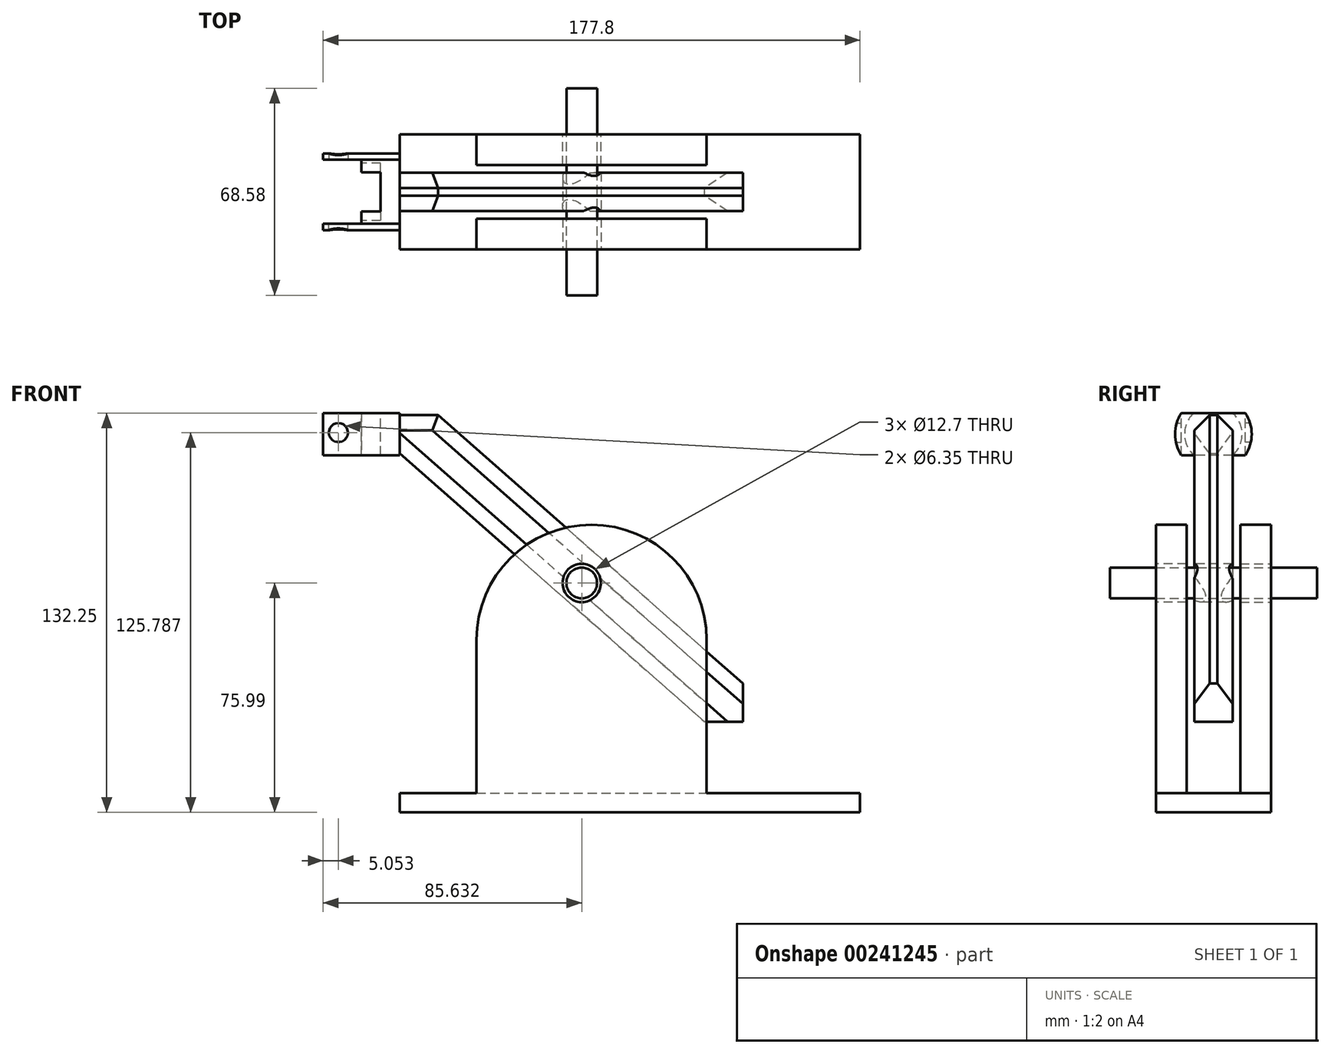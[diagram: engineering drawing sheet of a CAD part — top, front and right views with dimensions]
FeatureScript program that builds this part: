
annotation { "Feature Type Name" : "Feature", "Feature Type Description" : "" }
export const myFeature = defineFeature(function(context is Context, id is Id, definition is map)
    precondition{}
    {
        {
            var Q0;
            Q0=qCreatedBy(makeId("Front.planeOp"),FACE);
            var sketch = newSketch(context, id + "F0", { "sketchPlane" : qUnion([Q0])});
            skLineSegment(sketch, "E0.bottom", {"start": v(-76.2, 55.62) * mm, "end": v(37.4, 55.62) * mm});
            skLineSegment(sketch, "E0.top", {"start": v(-76.2, -45.98) * mm, "end": v(37.4, -45.98) * mm});
            skLineSegment(sketch, "E0.left", {"start": v(-76.2, 55.62) * mm, "end": v(-76.2, -45.98) * mm});
            skLineSegment(sketch, "E0.right", {"start": v(37.4, 55.62) * mm, "end": v(37.4, -45.98) * mm});
            skLineSegment(sketch, "E1", {"start": v(-76.2, 42.92) * mm, "end": v(24.7, -45.98) * mm});
            skLineSegment(sketch, "E2", {"start": v(37.4, -33.28) * mm, "end": v(-63.5, 55.62) * mm});
            skSolve(sketch);
        }
        {
            var Q0;
            {var subQ7=sQuery(id+"F0.wireOp",EDGE,"E1");Q0=makeQuery(id+"F0.imprint","IMPRINT",FACE,{"disambiguationData":[TD([[makeQuery(id+"F0.imprint","IMPRINT",EDGE,{"derivedFrom":subQ7}),1.0]])]});}
            extrude(context, id + "F1", {"entities" : qUnion([Q0]), "depth" : 12.7 * mm});
        }
        {
            var Q0;
            Q0=makeQuery(id+"F1.opExtrude","SWEPT_FACE",FACE,{"disambiguationData":[OSD([sQuery(id+"F0.wireOp",EDGE,"E0.left")])]});
            var sketch = newSketch(context, id + "F2", { "sketchPlane" : qUnion([Q0])});
            skLineSegment(sketch, "E3.bottom", {"start": v(0, 55.62) * mm, "end": v(12.7, 55.62) * mm});
            skLineSegment(sketch, "E3.top", {"start": v(0, 42.92) * mm, "end": v(12.7, 42.92) * mm});
            skLineSegment(sketch, "E3.left", {"start": v(0, 55.62) * mm, "end": v(0, 42.92) * mm});
            skLineSegment(sketch, "E3.right", {"start": v(12.7, 55.62) * mm, "end": v(12.7, 42.92) * mm});
            skSolve(sketch);
        }
        {
            var Q0;
            Q0 = qSketchRegion(id + "F2", true);
            extrude(context, id + "F3", {"entities" : qUnion([Q0]), "operationType" : NewBodyOperationType.ADD, "depth" : 12.7 * mm});
        }
        {
            var Q0;
            Q0=makeQuery(id+"F3.boolean.opBoolean","MERGE",FACE,{"derivedFrom":[makeQuery(id+"F1.opExtrude","CAP_FACE",FACE,{"disambiguationData":[OSD([sQuery(id+"F0.wireOp",EDGE,"E0.bottom"),sQuery(id+"F0.wireOp",EDGE,"E0.top"),sQuery(id+"F0.wireOp",EDGE,"E0.left"),sQuery(id+"F0.wireOp",EDGE,"E0.right"),sQuery(id+"F0.wireOp",EDGE,"E1"),sQuery(id+"F0.wireOp",EDGE,"E2")])],"isStart":true}),makeQuery(id+"F3.opExtrude","SWEPT_FACE",FACE,{"disambiguationData":[OSD([sQuery(id+"F2.wireOp",EDGE,"E3.left")])]})]});
            var sketch = newSketch(context, id + "F4", { "sketchPlane" : qUnion([Q0])});
            skLineSegment(sketch, "E4.bottom", {"start": v(76.2, 55.62) * mm, "end": v(88.9, 55.62) * mm});
            skLineSegment(sketch, "E4.top", {"start": v(76.2, 42.92) * mm, "end": v(88.9, 42.92) * mm});
            skLineSegment(sketch, "E4.left", {"start": v(76.2, 55.62) * mm, "end": v(76.2, 42.92) * mm});
            skLineSegment(sketch, "E4.right", {"start": v(88.9, 55.62) * mm, "end": v(88.9, 42.92) * mm});
            skSolve(sketch);
        }
        {
            var Q0;
            Q0 = qSketchRegion(id + "F4", true);
            extrude(context, id + "F5", {"entities" : qUnion([Q0]), "operationType" : NewBodyOperationType.ADD, "depth" : 6.35 * mm});
        }
        {
            var Q0;
            Q0=makeQuery(id+"F3.boolean.opBoolean","MERGE",FACE,{"derivedFrom":[makeQuery(id+"F1.opExtrude","CAP_FACE",FACE,{"disambiguationData":[OSD([sQuery(id+"F0.wireOp",EDGE,"E0.bottom"),sQuery(id+"F0.wireOp",EDGE,"E0.top"),sQuery(id+"F0.wireOp",EDGE,"E0.left"),sQuery(id+"F0.wireOp",EDGE,"E0.right"),sQuery(id+"F0.wireOp",EDGE,"E1"),sQuery(id+"F0.wireOp",EDGE,"E2")])],"isStart":false}),makeQuery(id+"F3.opExtrude","SWEPT_FACE",FACE,{"disambiguationData":[OSD([sQuery(id+"F2.wireOp",EDGE,"E3.right")])]})]});
            var sketch = newSketch(context, id + "F6", { "sketchPlane" : qUnion([Q0])});
            skLineSegment(sketch, "E5.bottom", {"start": v(-76.2, 55.62) * mm, "end": v(-88.9, 55.62) * mm});
            skLineSegment(sketch, "E5.top", {"start": v(-76.2, 42.92) * mm, "end": v(-88.9, 42.92) * mm});
            skLineSegment(sketch, "E5.left", {"start": v(-76.2, 55.62) * mm, "end": v(-76.2, 42.92) * mm});
            skLineSegment(sketch, "E5.right", {"start": v(-88.9, 55.62) * mm, "end": v(-88.9, 42.92) * mm});
            skSolve(sketch);
        }
        {
            var Q0;
            Q0 = qSketchRegion(id + "F6", true);
            extrude(context, id + "F7", {"entities" : qUnion([Q0]), "operationType" : NewBodyOperationType.ADD, "depth" : 6.35 * mm});
        }
        {
            var Q0;
            Q0=makeQuery(id+"F7.boolean.opBoolean","MERGE",FACE,{"derivedFrom":[makeQuery(id+"F5.boolean.opBoolean","MERGE",FACE,{"derivedFrom":[makeQuery(id+"F3.boolean.opBoolean","MERGE",FACE,{"derivedFrom":[makeQuery(id+"F1.opExtrude","SWEPT_FACE",FACE,{"disambiguationData":[OSD([sQuery(id+"F0.wireOp",EDGE,"E0.bottom")])]}),makeQuery(id+"F3.opExtrude","SWEPT_FACE",FACE,{"disambiguationData":[OSD([sQuery(id+"F2.wireOp",EDGE,"E3.bottom")])]})]}),makeQuery(id+"F5.opExtrude","SWEPT_FACE",FACE,{"disambiguationData":[OSD([sQuery(id+"F4.wireOp",EDGE,"E4.bottom")])]})]}),makeQuery(id+"F7.opExtrude","SWEPT_FACE",FACE,{"disambiguationData":[OSD([sQuery(id+"F6.wireOp",EDGE,"E5.bottom")])]})]});
            var sketch = newSketch(context, id + "F8", { "sketchPlane" : qUnion([Q0])});
            skLineSegment(sketch, "E6.bottom", {"start": v(-76.2, 6.35) * mm, "end": v(-88.9, 6.35) * mm});
            skLineSegment(sketch, "E6.top", {"start": v(-76.2, -19.05) * mm, "end": v(-88.9, -19.05) * mm});
            skLineSegment(sketch, "E6.left", {"start": v(-76.2, 6.35) * mm, "end": v(-76.2, -19.05) * mm});
            skLineSegment(sketch, "E6.right", {"start": v(-88.9, 6.35) * mm, "end": v(-88.9, -19.05) * mm});
            skSolve(sketch);
        }
        {
            var Q0;
            Q0 = qSketchRegion(id + "F8", true);
            extrude(context, id + "F9", {"entities" : qUnion([Q0]), "operationType" : NewBodyOperationType.ADD, "depth" : 6.35 * mm});
        }
        {
            var Q0;
            Q0=makeQuery(id+"F7.boolean.opBoolean","MERGE",FACE,{"derivedFrom":[makeQuery(id+"F5.boolean.opBoolean","MERGE",FACE,{"derivedFrom":[makeQuery(id+"F3.opExtrude","SWEPT_FACE",FACE,{"disambiguationData":[OSD([sQuery(id+"F2.wireOp",EDGE,"E3.top")])]}),makeQuery(id+"F5.opExtrude","SWEPT_FACE",FACE,{"disambiguationData":[OSD([sQuery(id+"F4.wireOp",EDGE,"E4.top")])]})]}),makeQuery(id+"F7.opExtrude","SWEPT_FACE",FACE,{"disambiguationData":[OSD([sQuery(id+"F6.wireOp",EDGE,"E5.top")])]})]});
            extrude(context, id + "F10", {"entities" : qUnion([Q0]), "operationType" : NewBodyOperationType.ADD, "depth" : 6.35 * mm});
        }
        {
            var Q0;
            {var subQ0=sQuery(id+"F6.wireOp",EDGE,"E5.right");var subQ1=sQuery(id+"F4.wireOp",EDGE,"E4.right");var subQ2=sQuery(id+"F2.wireOp",EDGE,"E3.top");Q0=makeQuery(id+"F10.boolean.opBoolean","MERGE",FACE,{"derivedFrom":[makeQuery(id+"F9.boolean.opBoolean","MERGE",FACE,{"derivedFrom":[makeQuery(id+"F7.boolean.opBoolean","MERGE",FACE,{"derivedFrom":[makeQuery(id+"F5.boolean.opBoolean","MERGE",FACE,{"derivedFrom":[makeQuery(id+"F3.opExtrude","CAP_FACE",FACE,{"disambiguationData":[OSD([sQuery(id+"F2.wireOp",EDGE,"E3.bottom"),subQ2,sQuery(id+"F2.wireOp",EDGE,"E3.left"),sQuery(id+"F2.wireOp",EDGE,"E3.right")])],"isStart":false}),makeQuery(id+"F5.opExtrude","SWEPT_FACE",FACE,{"disambiguationData":[OSD([subQ1])]})]}),makeQuery(id+"F7.opExtrude","SWEPT_FACE",FACE,{"disambiguationData":[OSD([subQ0])]})]}),makeQuery(id+"F9.opExtrude","SWEPT_FACE",FACE,{"disambiguationData":[OSD([sQuery(id+"F8.wireOp",EDGE,"E6.right")])]})]}),makeQuery(id+"F10.opExtrude","SWEPT_FACE",FACE,{"disambiguationData":[OSD([subQ2,sQuery(id+"F4.wireOp",EDGE,"E4.top"),subQ1,sQuery(id+"F6.wireOp",EDGE,"E5.top"),subQ0])]})]});}
            var sketch = newSketch(context, id + "F11", { "sketchPlane" : qUnion([Q0])});
            skCircle(sketch, "E7", {"center": v(6.35, 49.27) * mm, "radius": 12.7 * mm});
            skPoint(sketch, "E7.centerSnap0", {"position": v(6.35, 36.57) * mm});
            skSolve(sketch);
        }
        {
            var Q0;
            {var subQ0=sQuery(id+"F11.wireOp",EDGE,"E7");var subQ1=sQuery(id+"F8.wireOp",EDGE,"E6.right");var subQ2=makeQuery(id+"F9.opExtrude","CAP_EDGE",EDGE,{"disambiguationData":[OSD([subQ1])],"isStart":false});var subQ3=makeQuery(id+"F11.imprint","INTERSECT",VERTEX,{"derivedFrom":[subQ2,subQ0]});Q0=makeQuery(id+"F11.imprint","IMPRINT",FACE,{"disambiguationData":[TD([[makeQuery(id+"F11.imprint","IMPRINT",EDGE,{"disambiguationData":[TD([[subQ3,-1.0]])],"derivedFrom":subQ0}),-1.0]])]});}
            var Q1;
            {var subQ0=sQuery(id+"F11.wireOp",EDGE,"E7");var subQ1=sQuery(id+"F8.wireOp",EDGE,"E6.right");var subQ2=makeQuery(id+"F9.opExtrude","CAP_EDGE",EDGE,{"disambiguationData":[OSD([subQ1])],"isStart":false});var subQ3=makeQuery(id+"F11.imprint","INTERSECT",VERTEX,{"derivedFrom":[subQ2,subQ0]});Q1=makeQuery(id+"F11.imprint","IMPRINT",FACE,{"disambiguationData":[TD([[makeQuery(id+"F11.imprint","IMPRINT",EDGE,{"disambiguationData":[TD([[subQ3,1.0]])],"derivedFrom":subQ0}),-1.0]])]});}
            var Q2;
            {var subQ0=sQuery(id+"F11.wireOp",EDGE,"E7");var subQ1=sQuery(id+"F6.wireOp",EDGE,"E5.right");var subQ2=sQuery(id+"F6.wireOp",EDGE,"E5.top");var subQ3=makeQuery(id+"F10.boolean.opBoolean","MERGE",EDGE,{"derivedFrom":[makeQuery(id+"F9.boolean.opBoolean","MERGE",EDGE,{"derivedFrom":[makeQuery(id+"F7.opExtrude","CAP_EDGE",EDGE,{"disambiguationData":[OSD([subQ1])],"isStart":false}),makeQuery(id+"F9.opExtrude","SWEPT_EDGE",EDGE,{"disambiguationData":[OSD([sQuery(id+"F8.wireOp",EDGE,"E6.top"),sQuery(id+"F8.wireOp",EDGE,"E6.right")])]})]}),makeQuery(id+"F10.opExtrude","SWEPT_EDGE",EDGE,{"disambiguationData":[OSD([subQ2,subQ1])]})]});var subQ4=makeQuery(id+"F11.imprint","INTERSECT",VERTEX,{"derivedFrom":[subQ3,subQ0]});Q2=makeQuery(id+"F11.imprint","IMPRINT",FACE,{"disambiguationData":[TD([[makeQuery(id+"F11.imprint","IMPRINT",EDGE,{"disambiguationData":[TD([[subQ4,1.0]])],"derivedFrom":subQ0}),-1.0]])]});}
            var Q3;
            {var subQ0=sQuery(id+"F11.wireOp",EDGE,"E7");var subQ1=sQuery(id+"F4.wireOp",EDGE,"E4.right");var subQ2=sQuery(id+"F4.wireOp",EDGE,"E4.top");var subQ3=makeQuery(id+"F10.boolean.opBoolean","MERGE",EDGE,{"derivedFrom":[makeQuery(id+"F9.boolean.opBoolean","MERGE",EDGE,{"derivedFrom":[makeQuery(id+"F5.opExtrude","CAP_EDGE",EDGE,{"disambiguationData":[OSD([subQ1])],"isStart":false}),makeQuery(id+"F9.opExtrude","SWEPT_EDGE",EDGE,{"disambiguationData":[OSD([sQuery(id+"F8.wireOp",EDGE,"E6.bottom"),sQuery(id+"F8.wireOp",EDGE,"E6.right")])]})]}),makeQuery(id+"F10.opExtrude","SWEPT_EDGE",EDGE,{"disambiguationData":[OSD([subQ2,subQ1])]})]});var subQ4=makeQuery(id+"F11.imprint","INTERSECT",VERTEX,{"derivedFrom":[subQ3,subQ0]});Q3=makeQuery(id+"F11.imprint","IMPRINT",FACE,{"disambiguationData":[TD([[makeQuery(id+"F11.imprint","IMPRINT",EDGE,{"disambiguationData":[TD([[subQ4,-1.0]])],"derivedFrom":subQ0}),-1.0]])]});}
            extrude(context, id + "F12", {"entities" : qUnion([Q0, Q1, Q2, Q3]), "operationType" : NewBodyOperationType.REMOVE, "oppositeDirection" : true, "depth" : 12.7 * mm});
        }
        {
            var Q0;
            Q0=makeQuery(id+"F3.boolean.opBoolean","MERGE",EDGE,{"derivedFrom":[makeQuery(id+"F1.opExtrude","CAP_EDGE",EDGE,{"disambiguationData":[OSD([sQuery(id+"F0.wireOp",EDGE,"E0.bottom")])],"isStart":true}),makeQuery(id+"F3.opExtrude","SWEPT_EDGE",EDGE,{"disambiguationData":[OSD([sQuery(id+"F2.wireOp",EDGE,"E3.bottom"),sQuery(id+"F2.wireOp",EDGE,"E3.left")])]})]});
            var Q1;
            Q1=makeQuery(id+"F1.opExtrude","CAP_EDGE",EDGE,{"disambiguationData":[OSD([sQuery(id+"F0.wireOp",EDGE,"E2")])],"isStart":false});
            var Q2;
            Q2=makeQuery(id+"F3.boolean.opBoolean","MERGE",EDGE,{"derivedFrom":[makeQuery(id+"F1.opExtrude","CAP_EDGE",EDGE,{"disambiguationData":[OSD([sQuery(id+"F0.wireOp",EDGE,"E0.bottom")])],"isStart":false}),makeQuery(id+"F3.opExtrude","SWEPT_EDGE",EDGE,{"disambiguationData":[OSD([sQuery(id+"F2.wireOp",EDGE,"E3.bottom"),sQuery(id+"F2.wireOp",EDGE,"E3.right")])]})]});
            var Q3;
            Q3=makeQuery(id+"F1.opExtrude","CAP_EDGE",EDGE,{"disambiguationData":[OSD([sQuery(id+"F0.wireOp",EDGE,"E2")])],"isStart":true});
            var Q4;
            Q4=makeQuery(id+"F1.opExtrude","CAP_EDGE",EDGE,{"disambiguationData":[OSD([sQuery(id+"F0.wireOp",EDGE,"E1")])],"isStart":true});
            var Q5;
            Q5=makeQuery(id+"F1.opExtrude","CAP_EDGE",EDGE,{"disambiguationData":[OSD([sQuery(id+"F0.wireOp",EDGE,"E1")])],"isStart":false});
            chamfer(context, id + "F13", {"entities" : qUnion([Q0, Q1, Q2, Q3, Q4, Q5]), "width" : 5.08 * mm, "tangentPropagation" : true});
        }
        {
            var Q0;
            {var subQ0=sQuery(id+"F6.wireOp",EDGE,"E5.right");var subQ1=sQuery(id+"F4.wireOp",EDGE,"E4.right");var subQ2=sQuery(id+"F2.wireOp",EDGE,"E3.top");Q0=makeQuery(id+"F10.boolean.opBoolean","MERGE",FACE,{"derivedFrom":[makeQuery(id+"F9.boolean.opBoolean","MERGE",FACE,{"derivedFrom":[makeQuery(id+"F7.boolean.opBoolean","MERGE",FACE,{"derivedFrom":[makeQuery(id+"F5.boolean.opBoolean","MERGE",FACE,{"derivedFrom":[makeQuery(id+"F3.opExtrude","CAP_FACE",FACE,{"disambiguationData":[OSD([sQuery(id+"F2.wireOp",EDGE,"E3.bottom"),subQ2,sQuery(id+"F2.wireOp",EDGE,"E3.left"),sQuery(id+"F2.wireOp",EDGE,"E3.right")])],"isStart":false}),makeQuery(id+"F5.opExtrude","SWEPT_FACE",FACE,{"disambiguationData":[OSD([subQ1])]})]}),makeQuery(id+"F7.opExtrude","SWEPT_FACE",FACE,{"disambiguationData":[OSD([subQ0])]})]}),makeQuery(id+"F9.opExtrude","SWEPT_FACE",FACE,{"disambiguationData":[OSD([sQuery(id+"F8.wireOp",EDGE,"E6.right")])]})]}),makeQuery(id+"F10.opExtrude","SWEPT_FACE",FACE,{"disambiguationData":[OSD([subQ2,sQuery(id+"F4.wireOp",EDGE,"E4.top"),subQ1,sQuery(id+"F6.wireOp",EDGE,"E5.top"),subQ0])]})]});}
            var sketch = newSketch(context, id + "F14", { "sketchPlane" : qUnion([Q0])});
            skCircle(sketch, "E8", {"center": v(6.35, 49.27) * mm, "radius": 9.53 * mm});
            skSolve(sketch);
        }
        {
            var Q0;
            Q0=makeQuery(id+"F14.imprint","IMPRINT",FACE,{"disambiguationData":[TD([[makeQuery(id+"F14.imprint","IMPRINT",EDGE,{"derivedFrom":sQuery(id+"F14.wireOp",EDGE,"E8")}),1.0]])]});
            var sketch = newSketch(context, id + "F15", { "sketchPlane" : qUnion([Q0])});
            skSolve(sketch);
        }
        {
            var Q0;
            Q0 = qSketchRegion(id + "F15", true);
            var Q1;
            Q1=makeQuery(id+"F14.imprint","IMPRINT",FACE,{"disambiguationData":[TD([[makeQuery(id+"F14.imprint","IMPRINT",EDGE,{"derivedFrom":sQuery(id+"F14.wireOp",EDGE,"E8")}),1.0]])]});
            extrude(context, id + "F16", {"entities" : qUnion([Q0, Q1]), "operationType" : NewBodyOperationType.REMOVE, "oppositeDirection" : true, "depth" : 6.35 * mm});
        }
        {
            var Q0;
            {var subQ0=sQuery(id+"F6.wireOp",EDGE,"E5.right");var subQ1=sQuery(id+"F4.wireOp",EDGE,"E4.right");var subQ2=sQuery(id+"F2.wireOp",EDGE,"E3.top");Q0=makeQuery(id+"F10.boolean.opBoolean","MERGE",FACE,{"derivedFrom":[makeQuery(id+"F9.boolean.opBoolean","MERGE",FACE,{"derivedFrom":[makeQuery(id+"F7.boolean.opBoolean","MERGE",FACE,{"derivedFrom":[makeQuery(id+"F5.boolean.opBoolean","MERGE",FACE,{"derivedFrom":[makeQuery(id+"F3.opExtrude","CAP_FACE",FACE,{"disambiguationData":[OSD([sQuery(id+"F2.wireOp",EDGE,"E3.bottom"),subQ2,sQuery(id+"F2.wireOp",EDGE,"E3.left"),sQuery(id+"F2.wireOp",EDGE,"E3.right")])],"isStart":false}),makeQuery(id+"F5.opExtrude","SWEPT_FACE",FACE,{"disambiguationData":[OSD([subQ1])]})]}),makeQuery(id+"F7.opExtrude","SWEPT_FACE",FACE,{"disambiguationData":[OSD([subQ0])]})]}),makeQuery(id+"F9.opExtrude","SWEPT_FACE",FACE,{"disambiguationData":[OSD([sQuery(id+"F8.wireOp",EDGE,"E6.right")])]})]}),makeQuery(id+"F10.opExtrude","SWEPT_FACE",FACE,{"disambiguationData":[OSD([subQ2,sQuery(id+"F4.wireOp",EDGE,"E4.top"),subQ1,sQuery(id+"F6.wireOp",EDGE,"E5.top"),subQ0])]})]});}
            var sketch = newSketch(context, id + "F17", { "sketchPlane" : qUnion([Q0])});
            skLineSegment(sketch, "E9.bottom", {"start": v(-4.26, 56.26) * mm, "end": v(16.96, 56.26) * mm});
            skLineSegment(sketch, "E9.top", {"start": v(-4.26, 63.12) * mm, "end": v(16.96, 63.12) * mm});
            skLineSegment(sketch, "E9.left", {"start": v(-4.26, 56.26) * mm, "end": v(-4.26, 63.12) * mm});
            skLineSegment(sketch, "E9.right", {"start": v(16.96, 56.26) * mm, "end": v(16.96, 63.12) * mm});
            skLineSegment(sketch, "E10.bottom", {"start": v(-4.26, 42.29) * mm, "end": v(17.6, 42.29) * mm});
            skLineSegment(sketch, "E10.top", {"start": v(-4.26, 35.94) * mm, "end": v(17.6, 35.94) * mm});
            skLineSegment(sketch, "E10.left", {"start": v(-4.26, 42.29) * mm, "end": v(-4.26, 35.94) * mm});
            skLineSegment(sketch, "E10.right", {"start": v(17.6, 42.29) * mm, "end": v(17.6, 35.94) * mm});
            skSolve(sketch);
        }
        {
            var Q0;
            Q0 = qSketchRegion(id + "F17", true);
            extrude(context, id + "F18", {"entities" : qUnion([Q0]), "operationType" : NewBodyOperationType.REMOVE, "oppositeDirection" : true, "depth" : 12.7 * mm});
        }
        {
            var Q0;
            {var subQ0=sQuery(id+"F6.wireOp",EDGE,"E5.right");var subQ1=sQuery(id+"F4.wireOp",EDGE,"E4.right");var subQ2=sQuery(id+"F2.wireOp",EDGE,"E3.top");Q0=makeQuery(id+"F18.boolean.opBoolean","SPLIT",FACE,{"disambiguationData":[OD(0.0)],"derivedFrom":makeQuery(id+"F10.boolean.opBoolean","MERGE",FACE,{"derivedFrom":[makeQuery(id+"F9.boolean.opBoolean","MERGE",FACE,{"derivedFrom":[makeQuery(id+"F7.boolean.opBoolean","MERGE",FACE,{"derivedFrom":[makeQuery(id+"F5.boolean.opBoolean","MERGE",FACE,{"derivedFrom":[makeQuery(id+"F3.opExtrude","CAP_FACE",FACE,{"disambiguationData":[OSD([sQuery(id+"F2.wireOp",EDGE,"E3.bottom"),subQ2,sQuery(id+"F2.wireOp",EDGE,"E3.left"),sQuery(id+"F2.wireOp",EDGE,"E3.right")])],"isStart":false}),makeQuery(id+"F5.opExtrude","SWEPT_FACE",FACE,{"disambiguationData":[OSD([subQ1])]})]}),makeQuery(id+"F7.opExtrude","SWEPT_FACE",FACE,{"disambiguationData":[OSD([subQ0])]})]}),makeQuery(id+"F9.opExtrude","SWEPT_FACE",FACE,{"disambiguationData":[OSD([sQuery(id+"F8.wireOp",EDGE,"E6.right")])]})]}),makeQuery(id+"F10.opExtrude","SWEPT_FACE",FACE,{"disambiguationData":[OSD([subQ2,sQuery(id+"F4.wireOp",EDGE,"E4.top"),subQ1,sQuery(id+"F6.wireOp",EDGE,"E5.top"),subQ0])]})]})});}
            var Q1;
            {var subQ0=sQuery(id+"F6.wireOp",EDGE,"E5.right");var subQ1=sQuery(id+"F4.wireOp",EDGE,"E4.right");var subQ2=sQuery(id+"F2.wireOp",EDGE,"E3.top");Q1=makeQuery(id+"F18.boolean.opBoolean","SPLIT",FACE,{"disambiguationData":[OD(1.0)],"derivedFrom":makeQuery(id+"F10.boolean.opBoolean","MERGE",FACE,{"derivedFrom":[makeQuery(id+"F9.boolean.opBoolean","MERGE",FACE,{"derivedFrom":[makeQuery(id+"F7.boolean.opBoolean","MERGE",FACE,{"derivedFrom":[makeQuery(id+"F5.boolean.opBoolean","MERGE",FACE,{"derivedFrom":[makeQuery(id+"F3.opExtrude","CAP_FACE",FACE,{"disambiguationData":[OSD([sQuery(id+"F2.wireOp",EDGE,"E3.bottom"),subQ2,sQuery(id+"F2.wireOp",EDGE,"E3.left"),sQuery(id+"F2.wireOp",EDGE,"E3.right")])],"isStart":false}),makeQuery(id+"F5.opExtrude","SWEPT_FACE",FACE,{"disambiguationData":[OSD([subQ1])]})]}),makeQuery(id+"F7.opExtrude","SWEPT_FACE",FACE,{"disambiguationData":[OSD([subQ0])]})]}),makeQuery(id+"F9.opExtrude","SWEPT_FACE",FACE,{"disambiguationData":[OSD([sQuery(id+"F8.wireOp",EDGE,"E6.right")])]})]}),makeQuery(id+"F10.opExtrude","SWEPT_FACE",FACE,{"disambiguationData":[OSD([subQ2,sQuery(id+"F4.wireOp",EDGE,"E4.top"),subQ1,sQuery(id+"F6.wireOp",EDGE,"E5.top"),subQ0])]})]})});}
            extrude(context, id + "F19", {"entities" : qUnion([Q0, Q1]), "operationType" : NewBodyOperationType.ADD, "depth" : 12.7 * mm});
        }
        {
            var Q0;
            Q0=makeQuery(id+"F15.imprint","IMPRINT",FACE,{"disambiguationData":[TD([[makeQuery(id+"F15.imprint","IMPRINT",EDGE,{"derivedFrom":makeQuery(id+"F14.imprint","IMPRINT",EDGE,{"derivedFrom":sQuery(id+"F14.wireOp",EDGE,"E8")})}),1.0]])]});
            var sketch = newSketch(context, id + "F20", { "sketchPlane" : qUnion([Q0])});
            skLineSegment(sketch, "E11.bottom", {"start": v(-4.26, 56.26) * mm, "end": v(16.96, 56.26) * mm});
            skLineSegment(sketch, "E11.top", {"start": v(-4.26, 42.29) * mm, "end": v(16.96, 42.29) * mm});
            skLineSegment(sketch, "E11.left", {"start": v(-4.26, 56.26) * mm, "end": v(-4.26, 42.29) * mm});
            skLineSegment(sketch, "E11.right", {"start": v(16.96, 56.26) * mm, "end": v(16.96, 42.29) * mm});
            skSolve(sketch);
        }
        {
            var Q0;
            Q0 = qSketchRegion(id + "F20", true);
            extrude(context, id + "F21", {"entities" : qUnion([Q0]), "operationType" : NewBodyOperationType.REMOVE, "depth" : 14.22 * mm});
        }
        {
            var Q0;
            Q0=makeQuery(id+"F21.boolean.opBoolean","COPY",FACE,{"derivedFrom":makeQuery(id+"F21.opExtrude","SWEPT_FACE",FACE,{"disambiguationData":[OSD([sQuery(id+"F20.wireOp",EDGE,"E11.left")])]})});
            var sketch = newSketch(context, id + "F22", { "sketchPlane" : qUnion([Q0])});
            skCircle(sketch, "E12", {"center": v(-96.55, 49.8) * mm, "radius": 3.18 * mm});
            skSolve(sketch);
        }
        {
            var Q0;
            Q0 = qSketchRegion(id + "F22", true);
            extrude(context, id + "F23", {"entities" : qUnion([Q0]), "operationType" : NewBodyOperationType.REMOVE, "depth" : 25.4 * mm});
        }
        {
            var Q0;
            Q0=makeQuery(id+"F22.imprint","IMPRINT",FACE,{"disambiguationData":[TD([[makeQuery(id+"F22.imprint","IMPRINT",EDGE,{"derivedFrom":sQuery(id+"F22.wireOp",EDGE,"E12")}),1.0]])]});
            var Q1;
            Q1=sQuery(id+"F22.wireOp",EDGE,"E12");
            extrude(context, id + "F24", {"entities" : qUnion([Q0]), "operationType" : NewBodyOperationType.REMOVE, "surfaceEntities" : qUnion([Q1]), "oppositeDirection" : true, "depth" : 6.86 * mm});
        }
        {
            var Q0;
            Q0=makeQuery(id+"F3.boolean.opBoolean","MERGE",FACE,{"derivedFrom":[makeQuery(id+"F1.opExtrude","CAP_FACE",FACE,{"disambiguationData":[OSD([sQuery(id+"F0.wireOp",EDGE,"E0.bottom"),sQuery(id+"F0.wireOp",EDGE,"E0.top"),sQuery(id+"F0.wireOp",EDGE,"E0.left"),sQuery(id+"F0.wireOp",EDGE,"E0.right"),sQuery(id+"F0.wireOp",EDGE,"E1"),sQuery(id+"F0.wireOp",EDGE,"E2")])],"isStart":false}),makeQuery(id+"F3.opExtrude","SWEPT_FACE",FACE,{"disambiguationData":[OSD([sQuery(id+"F2.wireOp",EDGE,"E3.right")])]})]});
            var sketch = newSketch(context, id + "F25", { "sketchPlane" : qUnion([Q0])});
            skCircle(sketch, "E13", {"center": v(-15.97, 0) * mm, "radius": 6.35 * mm});
            skSolve(sketch);
        }
        {
            var Q0;
            Q0 = qSketchRegion(id + "F25", true);
            extrude(context, id + "F26", {"entities" : qUnion([Q0]), "operationType" : NewBodyOperationType.REMOVE, "oppositeDirection" : true, "depth" : 25.4 * mm});
        }
        {
            var Q0;
            Q0=qCreatedBy(makeId("Front.planeOp"),FACE);
            var sketch = newSketch(context, id + "F27", { "sketchPlane" : qUnion([Q0])});
            skLineSegment(sketch, "E14.bottom", {"start": v(76.2, -76) * mm, "end": v(-76.2, -76) * mm});
            skLineSegment(sketch, "E14.top", {"start": v(76.2, -69.64) * mm, "end": v(-76.2, -69.64) * mm});
            skLineSegment(sketch, "E14.left", {"start": v(76.2, -76) * mm, "end": v(76.2, -69.64) * mm});
            skLineSegment(sketch, "E14.right", {"start": v(-76.2, -76) * mm, "end": v(-76.2, -69.64) * mm});
            skSolve(sketch);
        }
        {
            var Q0;
            Q0 = qSketchRegion(id + "F27", true);
            extrude(context, id + "F28", {"entities" : qUnion([Q0]), "depth" : 25.4 * mm});
        }
        {
            var Q0;
            Q0=makeQuery(id+"F28.opExtrude","CAP_FACE",FACE,{"disambiguationData":[OSD([sQuery(id+"F27.wireOp",EDGE,"E14.bottom"),sQuery(id+"F27.wireOp",EDGE,"E14.top"),sQuery(id+"F27.wireOp",EDGE,"E14.left"),sQuery(id+"F27.wireOp",EDGE,"E14.right")])],"isStart":true});
            var sketch = newSketch(context, id + "F29", { "sketchPlane" : qUnion([Q0])});
            skSolve(sketch);
        }
        {
            var Q0;
            Q0 = qSketchRegion(id + "F29", true);
            var Q1;
            Q1=makeQuery(id+"F29.imprint","IMPRINT",FACE,{"disambiguationData":[TD([[makeQuery(id+"F29.imprint","IMPRINT",EDGE,{"derivedFrom":makeQuery(id+"F28.opExtrude","CAP_EDGE",EDGE,{"disambiguationData":[OSD([sQuery(id+"F27.wireOp",EDGE,"E14.bottom")])],"isStart":true})}),1.0]])]});
            extrude(context, id + "F30", {"entities" : qUnion([Q0, Q1]), "operationType" : NewBodyOperationType.ADD, "depth" : 12.7 * mm});
        }
        {
            var Q0;
            {var subQ0=sQuery(id+"F27.wireOp",EDGE,"E14.top");Q0=makeQuery(id+"F30.boolean.opBoolean","MERGE",FACE,{"derivedFrom":[makeQuery(id+"F28.opExtrude","SWEPT_FACE",FACE,{"disambiguationData":[OSD([subQ0])]}),makeQuery(id+"F30.opExtrude","SWEPT_FACE",FACE,{"disambiguationData":[OSD([subQ0])]})]});}
            var sketch = newSketch(context, id + "F31", { "sketchPlane" : qUnion([Q0])});
            skLineSegment(sketch, "E15.bottom", {"start": v(-50.8, 12.7) * mm, "end": v(25.4, 12.7) * mm});
            skLineSegment(sketch, "E15.top", {"start": v(-50.8, 2.54) * mm, "end": v(25.4, 2.54) * mm});
            skLineSegment(sketch, "E15.left", {"start": v(-50.8, 12.7) * mm, "end": v(-50.8, 2.54) * mm});
            skLineSegment(sketch, "E15.right", {"start": v(25.4, 12.7) * mm, "end": v(25.4, 2.54) * mm});
            skLineSegment(sketch, "E16.bottom", {"start": v(-50.8, -25.4) * mm, "end": v(25.4, -25.4) * mm});
            skLineSegment(sketch, "E16.top", {"start": v(-50.8, -15.24) * mm, "end": v(25.4, -15.24) * mm});
            skLineSegment(sketch, "E16.left", {"start": v(-50.8, -25.4) * mm, "end": v(-50.8, -15.24) * mm});
            skLineSegment(sketch, "E16.right", {"start": v(25.4, -25.4) * mm, "end": v(25.4, -15.24) * mm});
            skSolve(sketch);
        }
        {
            var Q0;
            Q0 = qSketchRegion(id + "F31", true);
            extrude(context, id + "F32", {"entities" : qUnion([Q0]), "operationType" : NewBodyOperationType.ADD, "depth" : 88.9 * mm});
        }
        {
            var Q0;
            {var subQ7=sQuery(id+"F0.wireOp",EDGE,"E1");Q0=makeQuery(id+"F0.imprint","IMPRINT",FACE,{"disambiguationData":[TD([[makeQuery(id+"F0.imprint","IMPRINT",EDGE,{"derivedFrom":subQ7}),1.0]])]});}
            var sketch = newSketch(context, id + "F33", { "sketchPlane" : qUnion([Q0])});
            skCircle(sketch, "E17", {"center": v(-15.97, 0) * mm, "radius": 5.08 * mm});
            skSolve(sketch);
        }
        {
            var Q0;
            Q0=makeQuery(id+"F33.imprint","IMPRINT",FACE,{"disambiguationData":[TD([[makeQuery(id+"F33.imprint","IMPRINT",EDGE,{"derivedFrom":sQuery(id+"F33.wireOp",EDGE,"E17")}),1.0]])]});
            extrude(context, id + "F34", {"entities" : qUnion([Q0]), "depth" : 25.4 * mm});
        }
        {
            var Q0;
            Q0=makeQuery(id+"F34.opExtrude","CAP_FACE",FACE,{"disambiguationData":[OSD([sQuery(id+"F33.wireOp",EDGE,"E17")])],"isStart":false});
            extrude(context, id + "F35", {"entities" : qUnion([Q0]), "operationType" : NewBodyOperationType.ADD, "oppositeDirection" : true, "depth" : 38.1 * mm});
        }
        {
            var Q0;
            Q0=makeQuery(id+"F32.boolean.opBoolean","MERGE",FACE,{"derivedFrom":[makeQuery(id+"F28.opExtrude","CAP_FACE",FACE,{"disambiguationData":[OSD([sQuery(id+"F27.wireOp",EDGE,"E14.bottom"),sQuery(id+"F27.wireOp",EDGE,"E14.top"),sQuery(id+"F27.wireOp",EDGE,"E14.left"),sQuery(id+"F27.wireOp",EDGE,"E14.right")])],"isStart":false}),makeQuery(id+"F32.opExtrude","SWEPT_FACE",FACE,{"disambiguationData":[OSD([sQuery(id+"F31.wireOp",EDGE,"E16.bottom")])]})]});
            var sketch = newSketch(context, id + "F36", { "sketchPlane" : qUnion([Q0])});
            skCircle(sketch, "E18", {"center": v(-15.97, 0) * mm, "radius": 6.35 * mm});
            skSolve(sketch);
        }
        {
            var Q0;
            Q0 = qSketchRegion(id + "F36", true);
            extrude(context, id + "F37", {"entities" : qUnion([Q0]), "operationType" : NewBodyOperationType.REMOVE, "oppositeDirection" : true, "depth" : 10.16 * mm});
        }
        {
            var Q0;
            Q0=makeQuery(id+"F37.boolean.opBoolean","COPY",FACE,{"derivedFrom":makeQuery(id+"F37.opExtrude","CAP_FACE",FACE,{"disambiguationData":[OSD([sQuery(id+"F36.wireOp",EDGE,"E18")])],"isStart":false})});
            extrude(context, id + "F38", {"entities" : qUnion([Q0]), "operationType" : NewBodyOperationType.ADD, "depth" : 25.4 * mm});
        }
        {
            var Q0;
            Q0=makeQuery(id+"F32.boolean.opBoolean","MERGE",FACE,{"derivedFrom":[makeQuery(id+"F30.opExtrude","CAP_FACE",FACE,{"disambiguationData":[OSD([sQuery(id+"F27.wireOp",EDGE,"E14.bottom"),sQuery(id+"F27.wireOp",EDGE,"E14.top"),sQuery(id+"F27.wireOp",EDGE,"E14.left"),sQuery(id+"F27.wireOp",EDGE,"E14.right")])],"isStart":false}),makeQuery(id+"F32.opExtrude","SWEPT_FACE",FACE,{"disambiguationData":[OSD([sQuery(id+"F31.wireOp",EDGE,"E15.bottom")])]})]});
            var sketch = newSketch(context, id + "F39", { "sketchPlane" : qUnion([Q0])});
            skCircle(sketch, "E19", {"center": v(15.97, 0) * mm, "radius": 6.35 * mm});
            skSolve(sketch);
        }
        {
            var Q0;
            Q0 = qSketchRegion(id + "F39", true);
            extrude(context, id + "F40", {"entities" : qUnion([Q0]), "operationType" : NewBodyOperationType.REMOVE, "oppositeDirection" : true, "depth" : 10.16 * mm});
        }
        {
            var Q0;
            Q0=makeQuery(id+"F40.boolean.opBoolean","COPY",FACE,{"derivedFrom":makeQuery(id+"F40.opExtrude","CAP_FACE",FACE,{"disambiguationData":[OSD([sQuery(id+"F39.wireOp",EDGE,"E19")])],"isStart":false})});
            extrude(context, id + "F41", {"entities" : qUnion([Q0]), "operationType" : NewBodyOperationType.ADD, "depth" : 25.4 * mm});
        }
        {
            var Q0;
            Q0=makeQuery(id+"F32.opExtrude","CAP_EDGE",EDGE,{"disambiguationData":[OSD([sQuery(id+"F31.wireOp",EDGE,"E16.right")])],"isStart":false});
            var Q1;
            Q1=makeQuery(id+"F32.opExtrude","CAP_EDGE",EDGE,{"disambiguationData":[OSD([sQuery(id+"F31.wireOp",EDGE,"E15.right")])],"isStart":false});
            var Q2;
            Q2=makeQuery(id+"F32.opExtrude","CAP_EDGE",EDGE,{"disambiguationData":[OSD([sQuery(id+"F31.wireOp",EDGE,"E16.left")])],"isStart":false});
            var Q3;
            Q3=makeQuery(id+"F32.opExtrude","CAP_EDGE",EDGE,{"disambiguationData":[OSD([sQuery(id+"F31.wireOp",EDGE,"E15.left")])],"isStart":false});
            fillet(context, id + "F42", {"entities" : qUnion([Q0, Q1, Q2, Q3]), "radius" : 38.1 * mm, "tangentPropagation" : true, "allowEdgeOverflow" : false});
        }
    });
